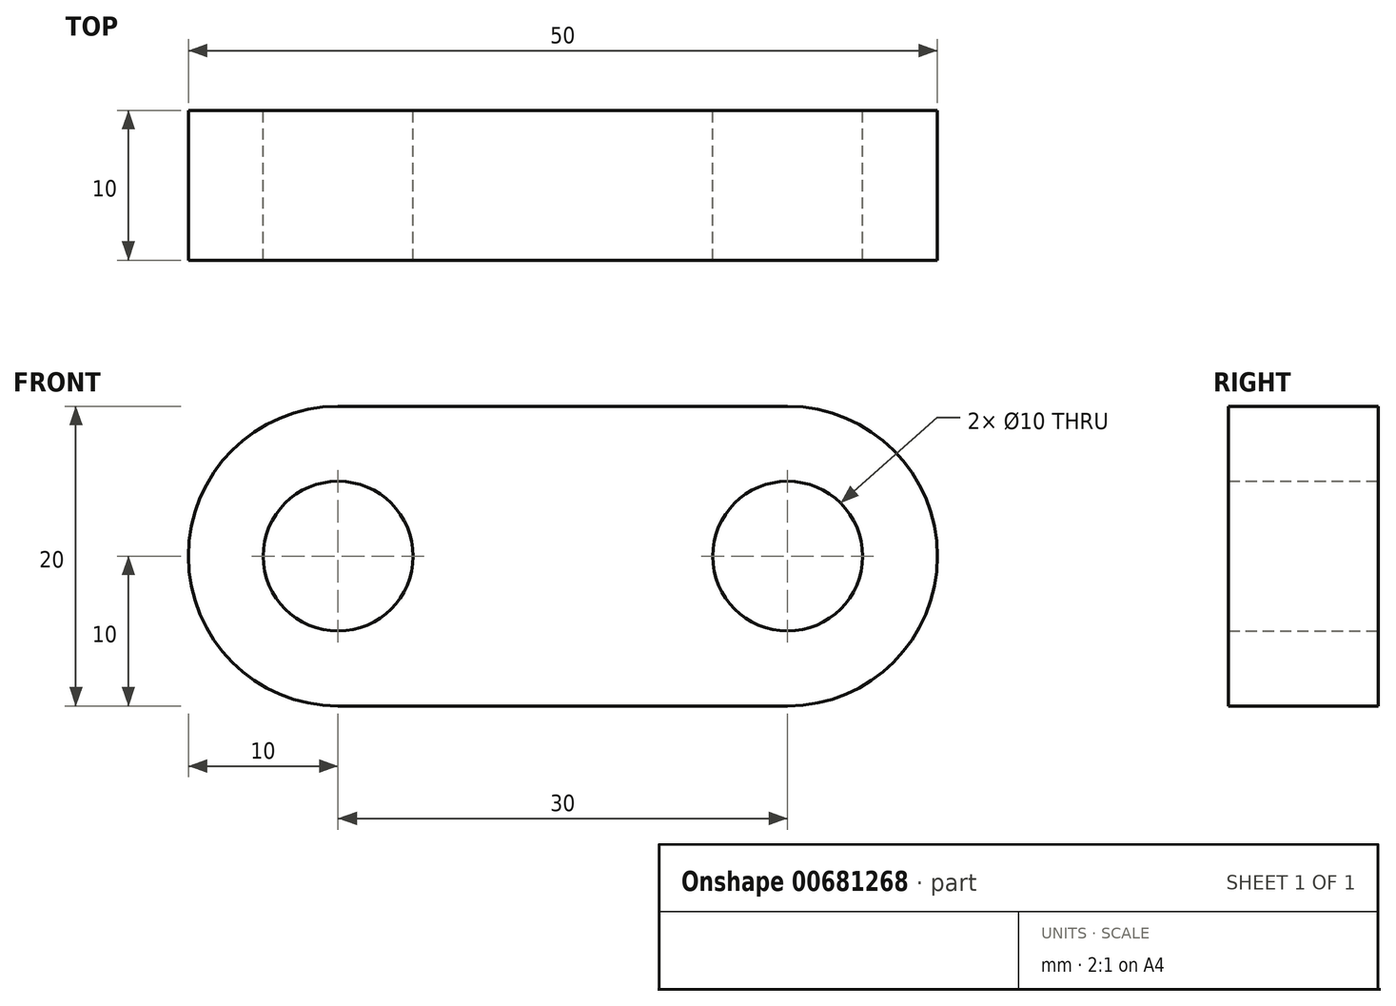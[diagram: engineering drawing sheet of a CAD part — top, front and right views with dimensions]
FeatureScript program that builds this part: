
annotation { "Feature Type Name" : "Feature", "Feature Type Description" : "" }
export const myFeature = defineFeature(function(context is Context, id is Id, definition is map)
    precondition{}
    {
        {
            var Q0;
            Q0=qCreatedBy(makeId("Front.planeOp"),FACE);
            var sketch = newSketch(context, id + "F0", { "sketchPlane" : qUnion([Q0])});
            skLineSegment(sketch, "E0.bottom", {"start": v(0, 10) * mm, "end": v(30, 10) * mm});
            skLineSegment(sketch, "E0.top", {"start": v(0, -10) * mm, "end": v(30, -10) * mm});
            skArc(sketch, "E1", {"start": v(0, 10) * mm, "mid": v(-10, 0) * mm, "end": v(0, -10) * mm});
            skArc(sketch, "E2", {"start": v(30, -10) * mm, "mid": v(40, 0) * mm, "end": v(30, 10) * mm});
            skCircle(sketch, "E3", {"center": v(0, 0) * mm, "radius": 5 * mm});
            skCircle(sketch, "E4", {"center": v(30, 0) * mm, "radius": 5 * mm});
            skSolve(sketch);
        }
        {
            var Q0;
            Q0=makeQuery(id+"F0.imprint","IMPRINT",FACE,{"disambiguationData":[TD([[makeQuery(id+"F0.imprint","IMPRINT",EDGE,{"derivedFrom":sQuery(id+"F0.wireOp",EDGE,"E0.bottom")}),-1.0]])]});
            extrude(context, id + "F1", {"entities" : qUnion([Q0]), "depth" : 10 * mm, "offsetDistance" : 25 * mm});
        }
    });
